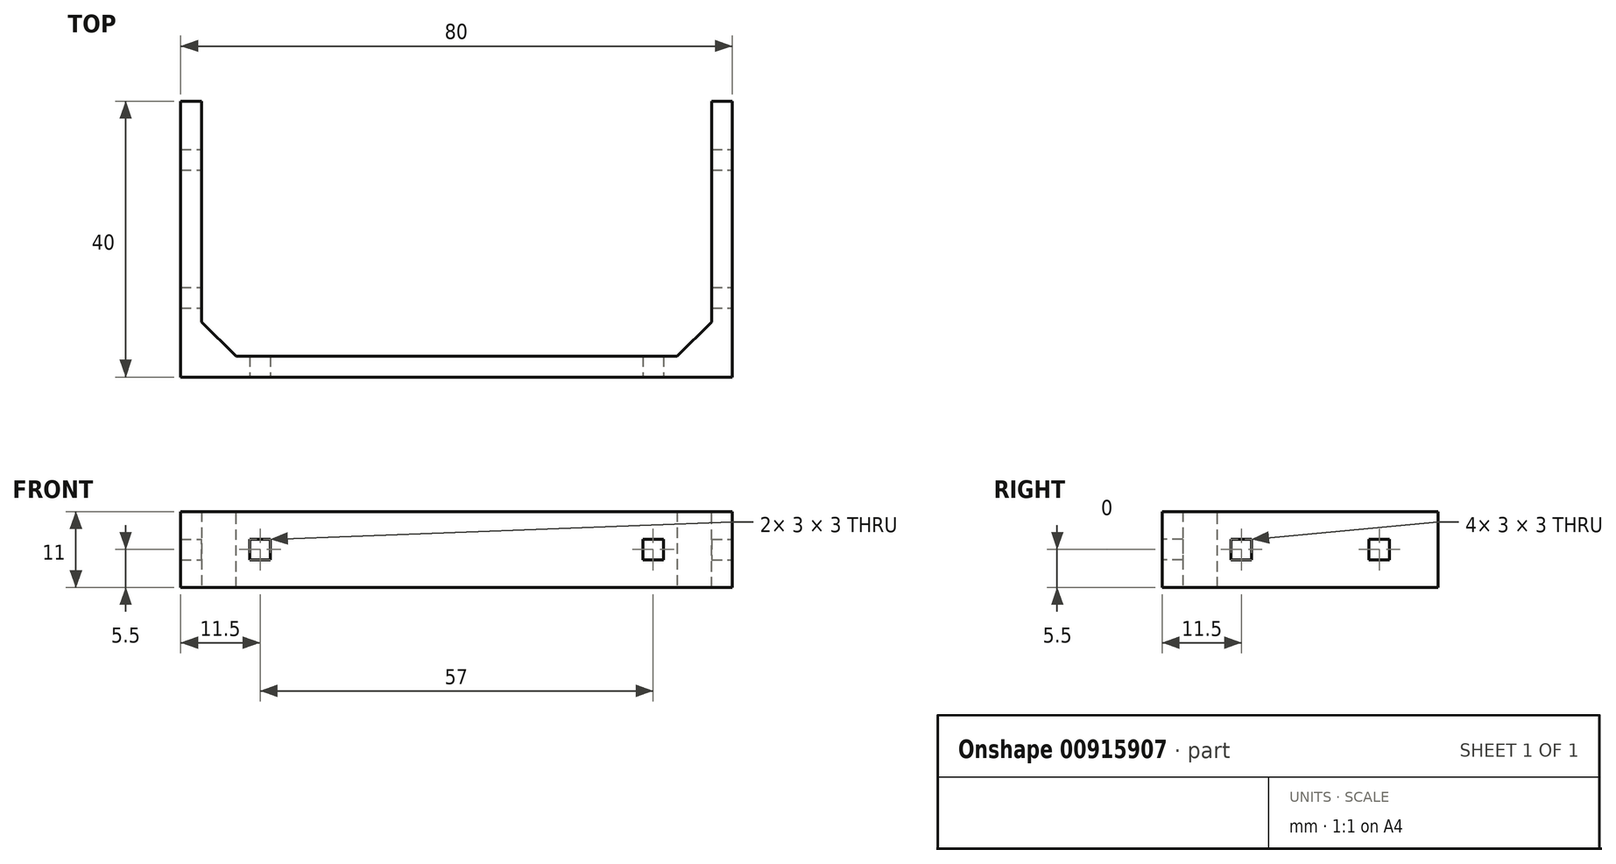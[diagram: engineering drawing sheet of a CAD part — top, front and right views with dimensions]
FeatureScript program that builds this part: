
annotation { "Feature Type Name" : "Feature", "Feature Type Description" : "" }
export const myFeature = defineFeature(function(context is Context, id is Id, definition is map)
    precondition{}
    {
        {
            var Q0;
            Q0=qCreatedBy(makeId("Front.planeOp"),FACE);
            var sketch = newSketch(context, id + "F0", { "sketchPlane" : qUnion([Q0])});
            skLineSegment(sketch, "E0", {"start": v(-40, 0) * mm, "end": v(40, 0) * mm});
            skLineSegment(sketch, "E1", {"start": v(40, 0) * mm, "end": v(40, 40) * mm});
            skLineSegment(sketch, "E2", {"start": v(40, 40) * mm, "end": v(37, 40) * mm});
            skLineSegment(sketch, "E3", {"start": v(37, 40) * mm, "end": v(37, 3) * mm});
            skLineSegment(sketch, "E4", {"start": v(37, 3) * mm, "end": v(-37, 3) * mm});
            skLineSegment(sketch, "E5", {"start": v(-37, 3) * mm, "end": v(-37, 40) * mm});
            skLineSegment(sketch, "E6", {"start": v(-37, 40) * mm, "end": v(-40, 40) * mm});
            skLineSegment(sketch, "E7", {"start": v(-40, 40) * mm, "end": v(-40, 0) * mm});
            skSolve(sketch);
        }
        {
            var Q0;
            Q0 = qSketchRegion(id + "F0", true);
            extrude(context, id + "F1", {"entities" : qUnion([Q0]), "depth" : 11 * mm, "offsetDistance" : 25 * mm});
        }
        {
            var Q0;
            Q0=makeQuery(id+"F1.opExtrude","SWEPT_EDGE",EDGE,{"disambiguationData":[OSD([sQuery(id+"F0.wireOp",EDGE,"E4"),sQuery(id+"F0.wireOp",EDGE,"E5")])]});
            var Q1;
            Q1=makeQuery(id+"F1.opExtrude","SWEPT_EDGE",EDGE,{"disambiguationData":[OSD([sQuery(id+"F0.wireOp",EDGE,"E3"),sQuery(id+"F0.wireOp",EDGE,"E4")])]});
            chamfer(context, id + "F2", {"entities" : qUnion([Q0, Q1]), "width" : 5 * mm, "tangentPropagation" : true});
        }
        {
            var Q0;
            Q0=qCreatedBy(makeId("Top.planeOp"),FACE);
            var sketch = newSketch(context, id + "F3", { "sketchPlane" : qUnion([Q0])});
            skLineSegment(sketch, "E8", {"start": v(0, 0) * mm, "end": v(67.02, 0) * mm});
            skSolve(sketch);
        }
        {
            var Q0;
            Q0=makeQuery(id+"F1.opExtrude","SWEPT_BODY",BODY,{"disambiguationData":[OSD([sQuery(id+"F0.wireOp",EDGE,"E0"),sQuery(id+"F0.wireOp",EDGE,"E1"),sQuery(id+"F0.wireOp",EDGE,"E2"),sQuery(id+"F0.wireOp",EDGE,"E3"),sQuery(id+"F0.wireOp",EDGE,"E4"),sQuery(id+"F0.wireOp",EDGE,"E5"),sQuery(id+"F0.wireOp",EDGE,"E6"),sQuery(id+"F0.wireOp",EDGE,"E7")])]});
            var Q1;
            Q1=sQuery(id+"F3.wireOp",EDGE,"E8");
            transform(context, id + "F4", {"entities" : qUnion([Q0]), "transformType" : TransformType.ROTATION, "transformAxis" : qUnion([Q1]), "angle" : 90 * degree, "oppositeDirection" : true, "makeCopy" : false});
        }
        {
            var Q0;
            Q0=makeQuery(id+"F1.opExtrude","SWEPT_FACE",FACE,{"disambiguationData":[OSD([sQuery(id+"F0.wireOp",EDGE,"E1")])]});
            var sketch = newSketch(context, id + "F5", { "sketchPlane" : qUnion([Q0])});
            skLineSegment(sketch, "E9.bottom", {"start": v(10, 7) * mm, "end": v(13, 7) * mm});
            skLineSegment(sketch, "E9.top", {"start": v(10, 4) * mm, "end": v(13, 4) * mm});
            skLineSegment(sketch, "E9.left", {"start": v(10, 7) * mm, "end": v(10, 4) * mm});
            skLineSegment(sketch, "E9.right", {"start": v(13, 7) * mm, "end": v(13, 4) * mm});
            skLineSegment(sketch, "E10.bottom", {"start": v(30, 7) * mm, "end": v(33, 7) * mm});
            skLineSegment(sketch, "E10.top", {"start": v(30, 4) * mm, "end": v(33, 4) * mm});
            skLineSegment(sketch, "E10.left", {"start": v(30, 7) * mm, "end": v(30, 4) * mm});
            skLineSegment(sketch, "E10.right", {"start": v(33, 7) * mm, "end": v(33, 4) * mm});
            skSolve(sketch);
        }
        {
            var Q0;
            Q0 = qSketchRegion(id + "F5", true);
            extrude(context, id + "F6", {"entities" : qUnion([Q0]), "operationType" : NewBodyOperationType.REMOVE, "endBound" : BoundingType.THROUGH_ALL, "oppositeDirection" : true, "depth" : 25 * mm, "offsetDistance" : 25 * mm});
        }
        {
            var Q0;
            Q0=makeQuery(id+"F1.opExtrude","SWEPT_FACE",FACE,{"disambiguationData":[OSD([sQuery(id+"F0.wireOp",EDGE,"E0")])]});
            var sketch = newSketch(context, id + "F7", { "sketchPlane" : qUnion([Q0])});
            skLineSegment(sketch, "E11.bottom", {"start": v(-30, 7) * mm, "end": v(-27, 7) * mm});
            skLineSegment(sketch, "E11.top", {"start": v(-30, 4) * mm, "end": v(-27, 4) * mm});
            skLineSegment(sketch, "E11.left", {"start": v(-30, 7) * mm, "end": v(-30, 4) * mm});
            skLineSegment(sketch, "E11.right", {"start": v(-27, 7) * mm, "end": v(-27, 4) * mm});
            skLineSegment(sketch, "E12.bottom", {"start": v(30, 7) * mm, "end": v(27, 7) * mm});
            skLineSegment(sketch, "E12.top", {"start": v(30, 4) * mm, "end": v(27, 4) * mm});
            skLineSegment(sketch, "E12.left", {"start": v(30, 7) * mm, "end": v(30, 4) * mm});
            skLineSegment(sketch, "E12.right", {"start": v(27, 7) * mm, "end": v(27, 4) * mm});
            skSolve(sketch);
        }
        {
            var Q0;
            Q0 = qSketchRegion(id + "F7", true);
            extrude(context, id + "F8", {"entities" : qUnion([Q0]), "operationType" : NewBodyOperationType.REMOVE, "oppositeDirection" : true, "depth" : 25 * mm, "offsetDistance" : 25 * mm});
        }
    });
